# Revit family: Shower-Digital_Valve-KOHLER-DTV-K-682_1
name_source: partatom
category: Plumbing Fixtures
revit_build: Autodesk Revit 2017 (Build: 20160225_1515(x64)
units: mm (PartAtom-declared; Revit-internal decimal feet)

## family parameters
Cut with Voids When Loaded = No
Host = Face
OmniClass Number = 23.27.31.00
OmniClass Title = Valves
Part Type = Normal
Room Calculation Point = No
Round Connector Dimension = Use Diameter
Shared = No

## types (1)
- NA-Stainless
    ADA Compliant = No
    Apparent Load = 1650 VA
    Assembly Code = D2020
    CW Connection = Yes
    Cold Water Inlet = Cold Water Inlet
    Cold Water Inlet 1 = Cold Water Inlet 1
    Date Modified = 09/24/2020
    Default Elevation = 42"
    Description = six-port thermostatic valve
    Electrical Connector = Yes
    Electrical Note = Dedicated Circuit Required Protected With Class A Ground Fault Circuit Interrupter (GFCI) Or Residual Current Device(RCD)
    Finish = Kohler-Metal-NA-Stainless
    Flow Rate = 21 GPM
    HW Connection = Yes
    Height = 3 5/16"
    Hot Water Inlet = Hot Water Inlet
    Length = 9 3/16"
    Manufacturer = KOHLER Co.
    Master Format 2014 = 23 09 13.33
    Master Format 2014 Name = Control Valves
    Material = Brass Construction
    Model = K-682-K-NA
    Pressure = 45.00 psi
    Product Documentation Link = https://www.us.kohler.com
    Product Name = DTV
    Product Page URL = http://www.us.kohler.com
    Tempered Water Outlet 1 = Tempered Water Outlet 1
    Tempered Water Outlet 2 = Tempered Water Outlet 2
    Tempered Water Outlet 3 = Tempered Water Outlet 3
    Tempered Water Outlet 4 = Tempered Water Outlet 4
    Tempered Water Outlet 5 = Tempered Water Outlet 5
    Tempered Water Outlet 6 = Tempered Water Outlet 6
    Type = 1
    URL = https://www.us.kohler.com
    Vent Connection = No
    Voltage = 120 V
    Waste Connection = No
    Waste Water Outlet = Waste Water Outlet
    WaterSense Certified = No
    Width = 22 1/4"

## geometry (parser evidence)
native form markers: Sweep x5
no freeform markers — native parametric forms only
